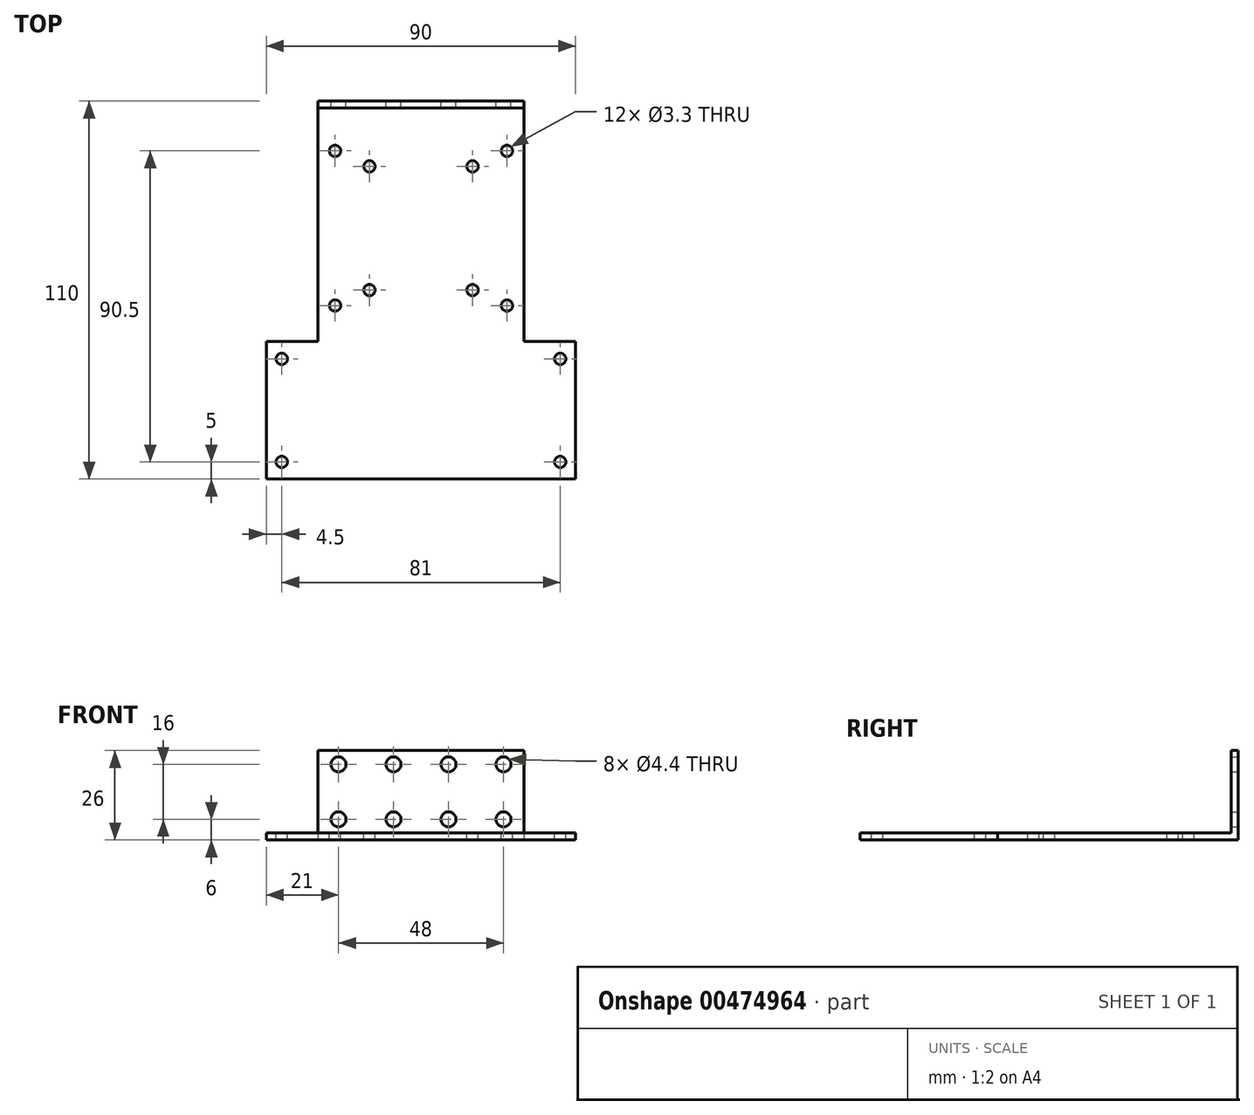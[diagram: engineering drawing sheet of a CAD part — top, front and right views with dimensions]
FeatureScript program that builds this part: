
annotation { "Feature Type Name" : "Feature", "Feature Type Description" : "" }
export const myFeature = defineFeature(function(context is Context, id is Id, definition is map)
    precondition{}
    {
        {
            var Q0;
            Q0=qCreatedBy(makeId("Top.planeOp"),FACE);
            var sketch = newSketch(context, id + "F0", { "sketchPlane" : qUnion([Q0])});
            skLineSegment(sketch, "E0.bottom", {"start": v(-45, 55) * mm, "end": v(45, 55) * mm});
            skLineSegment(sketch, "E0.top", {"start": v(-45, -55) * mm, "end": v(45, -55) * mm});
            skLineSegment(sketch, "E0.left", {"start": v(-45, 55) * mm, "end": v(-45, -55) * mm});
            skLineSegment(sketch, "E0.right", {"start": v(45, 55) * mm, "end": v(45, -55) * mm});
            skSolve(sketch);
        }
        {
            var Q0;
            Q0=makeQuery(id+"F0.imprint","IMPRINT",FACE,{"disambiguationData":[TD([[makeQuery(id+"F0.imprint","IMPRINT",EDGE,{"derivedFrom":sQuery(id+"F0.wireOp",EDGE,"E0.bottom")}),-1.0]])]});
            extrude(context, id + "F1", {"entities" : qUnion([Q0]), "depth" : 26 * mm});
        }
        {
            var Q0;
            Q0=makeQuery(id+"F1.opExtrude","SWEPT_FACE",FACE,{"disambiguationData":[OSD([sQuery(id+"F0.wireOp",EDGE,"E0.right")])]});
            var sketch = newSketch(context, id + "F2", { "sketchPlane" : qUnion([Q0])});
            skLineSegment(sketch, "E1.bottom", {"start": v(-55, 26) * mm, "end": v(53, 26) * mm});
            skLineSegment(sketch, "E1.top", {"start": v(-55, 2) * mm, "end": v(53, 2) * mm});
            skLineSegment(sketch, "E1.left", {"start": v(-55, 26) * mm, "end": v(-55, 2) * mm});
            skLineSegment(sketch, "E1.right", {"start": v(53, 26) * mm, "end": v(53, 2) * mm});
            skSolve(sketch);
        }
        {
            var Q0;
            Q0 = qSketchRegion(id + "F2", true);
            extrude(context, id + "F3", {"entities" : qUnion([Q0]), "operationType" : NewBodyOperationType.REMOVE, "endBound" : BoundingType.THROUGH_ALL, "oppositeDirection" : true, "depth" : 25 * mm});
        }
        {
            var Q0;
            Q0=makeQuery(id+"F1.opExtrude","SWEPT_FACE",FACE,{"disambiguationData":[OSD([sQuery(id+"F0.wireOp",EDGE,"E0.bottom")])]});
            var sketch = newSketch(context, id + "F4", { "sketchPlane" : qUnion([Q0])});
            skPoint(sketch, "E2", {"position": v(-8, 22) * mm});
            skPoint(sketch, "E3", {"position": v(8, 22) * mm});
            skPoint(sketch, "E4", {"position": v(8, 6) * mm});
            skPoint(sketch, "E5", {"position": v(-8, 6) * mm});
            skPoint(sketch, "E6", {"position": v(-24, 22) * mm});
            skPoint(sketch, "E7", {"position": v(-24, 6) * mm});
            skPoint(sketch, "E8", {"position": v(24, 22) * mm});
            skPoint(sketch, "E9", {"position": v(24, 6) * mm});
            skSolve(sketch);
        }
        {
            var Q0;
            Q0=sQuery(id+"F4.wireOp",VERTEX,"E2");
            var Q1;
            Q1=sQuery(id+"F4.wireOp",VERTEX,"E3");
            var Q2;
            Q2=sQuery(id+"F4.wireOp",VERTEX,"E4");
            var Q3;
            Q3=sQuery(id+"F4.wireOp",VERTEX,"E5");
            var Q4;
            Q4=sQuery(id+"F4.wireOp",VERTEX,"E6");
            var Q5;
            Q5=sQuery(id+"F4.wireOp",VERTEX,"E8");
            var Q6;
            Q6=sQuery(id+"F4.wireOp",VERTEX,"E9");
            var Q7;
            Q7=sQuery(id+"F4.wireOp",VERTEX,"E7");
            var Q8;
            Q8=makeQuery(id+"F1.opExtrude","SWEPT_BODY",BODY,{"disambiguationData":[OSD([sQuery(id+"F0.wireOp",EDGE,"E0.bottom"),sQuery(id+"F0.wireOp",EDGE,"E0.top"),sQuery(id+"F0.wireOp",EDGE,"E0.left"),sQuery(id+"F0.wireOp",EDGE,"E0.right")])]});
            hole(context, id + "F5", {"style" : HoleStyle.SIMPLE, "endStyle" : HoleEndStyle.THROUGH, "standardTappedOrClearance" : lookupTablePath({ "standard" : "ISO", "fit" : "Normal", "size" : "M4", "type" : "Clearance" }), "standardBlindInLast" : lookupTablePath({ "fit" : "Standard", "standard" : "ISO", "size" : "M4", "type" : "Clearance" }), "holeDiameter" : 4.4 * mm, "isTappedThrough" : true, "tappedDepth" : 12 * mm, "tapClearance" : 3, "locations" : qUnion([Q0, Q1, Q2, Q3, Q4, Q5, Q6, Q7]), "scope" : qUnion([Q8])});
        }
        {
            var Q0;
            Q0=makeQuery(id+"F1.opExtrude","CAP_FACE",FACE,{"disambiguationData":[OSD([sQuery(id+"F0.wireOp",EDGE,"E0.bottom"),sQuery(id+"F0.wireOp",EDGE,"E0.top"),sQuery(id+"F0.wireOp",EDGE,"E0.left"),sQuery(id+"F0.wireOp",EDGE,"E0.right")])],"isStart":true});
            var sketch = newSketch(context, id + "F6", { "sketchPlane" : qUnion([Q0])});
            skLineSegment(sketch, "E10.bottom", {"start": v(-45, -55) * mm, "end": v(-30, -55) * mm});
            skLineSegment(sketch, "E10.top", {"start": v(-45, 15) * mm, "end": v(-30, 15) * mm});
            skLineSegment(sketch, "E10.left", {"start": v(-45, -55) * mm, "end": v(-45, 15) * mm});
            skLineSegment(sketch, "E10.right", {"start": v(-30, -55) * mm, "end": v(-30, 15) * mm});
            skLineSegment(sketch, "E11.bottom", {"start": v(45, -55) * mm, "end": v(30, -55) * mm});
            skLineSegment(sketch, "E11.top", {"start": v(45, 15) * mm, "end": v(30, 15) * mm});
            skLineSegment(sketch, "E11.left", {"start": v(45, -55) * mm, "end": v(45, 15) * mm});
            skLineSegment(sketch, "E11.right", {"start": v(30, -55) * mm, "end": v(30, 15) * mm});
            skSolve(sketch);
        }
        {
            var Q0;
            Q0=makeQuery(id+"F6.imprint","IMPRINT",FACE,{"disambiguationData":[TD([[makeQuery(id+"F6.imprint","IMPRINT",EDGE,{"derivedFrom":sQuery(id+"F6.wireOp",EDGE,"E10.bottom")}),1.0]])]});
            var Q1;
            Q1=makeQuery(id+"F6.imprint","IMPRINT",FACE,{"disambiguationData":[TD([[makeQuery(id+"F6.imprint","IMPRINT",EDGE,{"derivedFrom":sQuery(id+"F6.wireOp",EDGE,"E11.bottom")}),1.0]])]});
            extrude(context, id + "F7", {"entities" : qUnion([Q0, Q1]), "operationType" : NewBodyOperationType.REMOVE, "endBound" : BoundingType.THROUGH_ALL, "oppositeDirection" : true, "depth" : 25 * mm});
        }
        {
            var Q0;
            Q0=makeQuery(id+"F3.boolean.opBoolean","COPY",FACE,{"derivedFrom":makeQuery(id+"F3.opExtrude","SWEPT_FACE",FACE,{"disambiguationData":[OSD([sQuery(id+"F2.wireOp",EDGE,"E1.top")])]})});
            var sketch = newSketch(context, id + "F8", { "sketchPlane" : qUnion([Q0])});
            skPoint(sketch, "E12", {"position": v(-40.5, -50) * mm});
            skPoint(sketch, "E13", {"position": v(-40.5, -20) * mm});
            skPoint(sketch, "E14", {"position": v(40.5, -20) * mm});
            skPoint(sketch, "E15", {"position": v(40.5, -50) * mm});
            skPoint(sketch, "E16", {"position": v(-25, -4.5) * mm});
            skPoint(sketch, "E17", {"position": v(25, -4.5) * mm});
            skPoint(sketch, "E18", {"position": v(-25, 40.5) * mm});
            skPoint(sketch, "E19", {"position": v(25, 40.5) * mm});
            skPoint(sketch, "E20", {"position": v(-15, 36) * mm});
            skPoint(sketch, "E21", {"position": v(15, 36) * mm});
            skPoint(sketch, "E22", {"position": v(15, 0) * mm});
            skPoint(sketch, "E23", {"position": v(-15, 0) * mm});
            skSolve(sketch);
        }
        {
            var Q0;
            Q0=sQuery(id+"F8.wireOp",VERTEX,"E19");
            var Q1;
            Q1=sQuery(id+"F8.wireOp",VERTEX,"E21");
            var Q2;
            Q2=sQuery(id+"F8.wireOp",VERTEX,"E20");
            var Q3;
            Q3=sQuery(id+"F8.wireOp",VERTEX,"E18");
            var Q4;
            Q4=sQuery(id+"F8.wireOp",VERTEX,"E16");
            var Q5;
            Q5=sQuery(id+"F8.wireOp",VERTEX,"E23");
            var Q6;
            Q6=sQuery(id+"F8.wireOp",VERTEX,"E22");
            var Q7;
            Q7=sQuery(id+"F8.wireOp",VERTEX,"E17");
            var Q8;
            Q8=sQuery(id+"F8.wireOp",VERTEX,"E14");
            var Q9;
            Q9=sQuery(id+"F8.wireOp",VERTEX,"E15");
            var Q10;
            Q10=sQuery(id+"F8.wireOp",VERTEX,"E12");
            var Q11;
            Q11=sQuery(id+"F8.wireOp",VERTEX,"E13");
            var Q12;
            Q12=makeQuery(id+"F1.opExtrude","SWEPT_BODY",BODY,{"disambiguationData":[OSD([sQuery(id+"F0.wireOp",EDGE,"E0.bottom"),sQuery(id+"F0.wireOp",EDGE,"E0.top"),sQuery(id+"F0.wireOp",EDGE,"E0.left"),sQuery(id+"F0.wireOp",EDGE,"E0.right")])]});
            hole(context, id + "F9", {"style" : HoleStyle.SIMPLE, "endStyle" : HoleEndStyle.THROUGH, "standardTappedOrClearance" : lookupTablePath({ "standard" : "ISO", "fit" : "Normal", "size" : "M3", "type" : "Clearance" }), "standardBlindInLast" : lookupTablePath({ "fit" : "Standard", "standard" : "ISO", "size" : "M3", "type" : "Clearance" }), "holeDiameter" : 3.3 * mm, "isTappedThrough" : true, "tappedDepth" : 12 * mm, "tapClearance" : 3, "locations" : qUnion([Q0, Q1, Q2, Q3, Q4, Q5, Q6, Q7, Q8, Q9, Q10, Q11]), "scope" : qUnion([Q12])});
        }
    });
